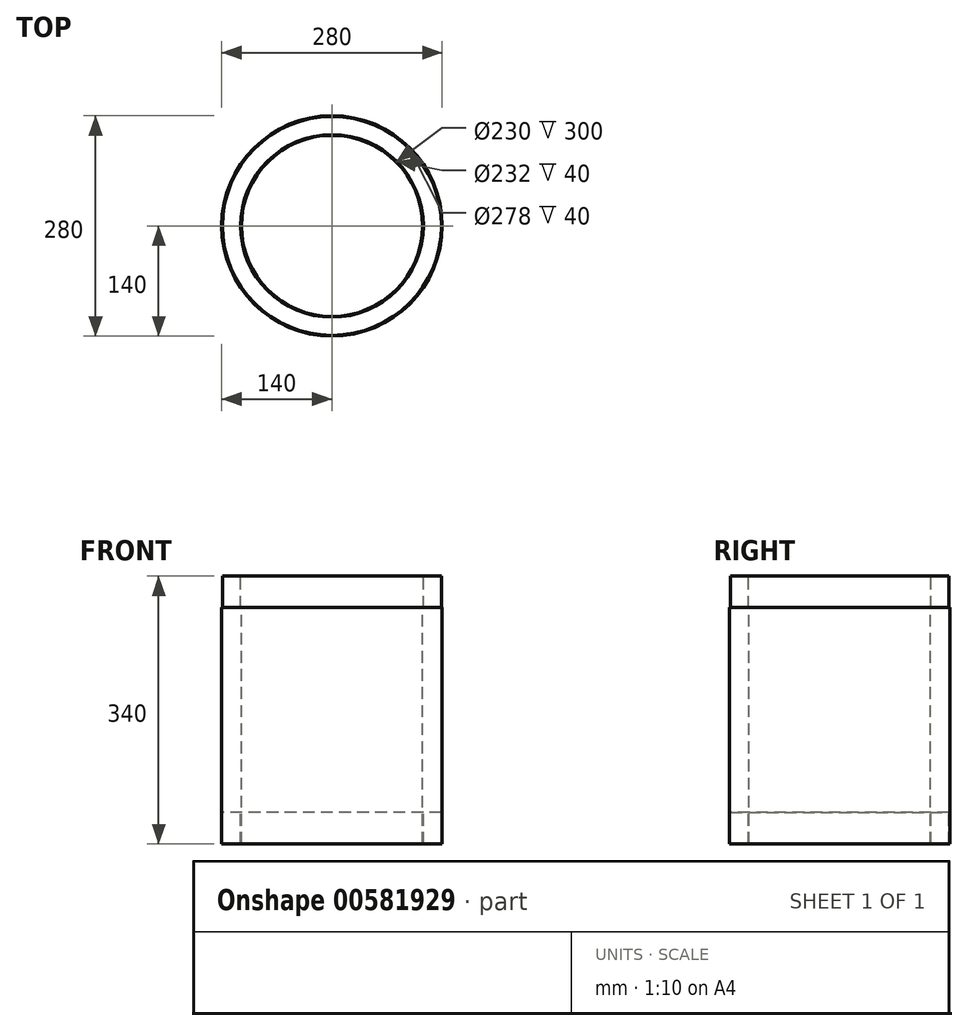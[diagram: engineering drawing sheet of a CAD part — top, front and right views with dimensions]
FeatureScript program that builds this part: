
annotation { "Feature Type Name" : "Feature", "Feature Type Description" : "" }
export const myFeature = defineFeature(function(context is Context, id is Id, definition is map)
    precondition{}
    {
        {
            var Q0;
            Q0=qCreatedBy(makeId("Front.planeOp"),FACE);
            var sketch = newSketch(context, id + "F0", { "sketchPlane" : qUnion([Q0])});
            skLineSegment(sketch, "E0", {"start": v(0, 345.75) * mm, "end": v(0, -558.03) * mm, "construction": true});
            skLineSegment(sketch, "E1", {"start": v(-115, -518.84) * mm, "end": v(-115, -218.84) * mm});
            skLineSegment(sketch, "E2", {"start": v(-115, -218.84) * mm, "end": v(-116, -218.84) * mm});
            skLineSegment(sketch, "E3", {"start": v(-116, -218.84) * mm, "end": v(-116, -178.84) * mm});
            skLineSegment(sketch, "E4", {"start": v(-116, -178.84) * mm, "end": v(-139, -178.84) * mm});
            skLineSegment(sketch, "E5", {"start": v(-139, -178.84) * mm, "end": v(-139, -218.84) * mm});
            skLineSegment(sketch, "E6", {"start": v(-139, -218.84) * mm, "end": v(-140, -218.84) * mm});
            skLineSegment(sketch, "E7", {"start": v(-140, -218.84) * mm, "end": v(-140, -518.84) * mm});
            skLineSegment(sketch, "E8", {"start": v(-140, -518.84) * mm, "end": v(-139, -518.84) * mm});
            skLineSegment(sketch, "E9", {"start": v(-139, -518.84) * mm, "end": v(-139, -478.84) * mm});
            skLineSegment(sketch, "E10", {"start": v(-139, -478.84) * mm, "end": v(-116, -478.84) * mm});
            skLineSegment(sketch, "E11", {"start": v(-116, -478.84) * mm, "end": v(-116, -518.84) * mm});
            skLineSegment(sketch, "E12", {"start": v(-116, -518.84) * mm, "end": v(-115, -518.84) * mm});
            skSolve(sketch);
        }
        {
            var Q0;
            Q0=qSketchRegion(id+"F0",true);
            var Q1;
            Q1=sQuery(id+"F0.wireOp",EDGE,"E0");
            revolve(context, id + "F1", {"entities" : qUnion([Q0]), "axis" : qUnion([Q1]), "revolveType" : RevolveType.FULL});
        }
    });
